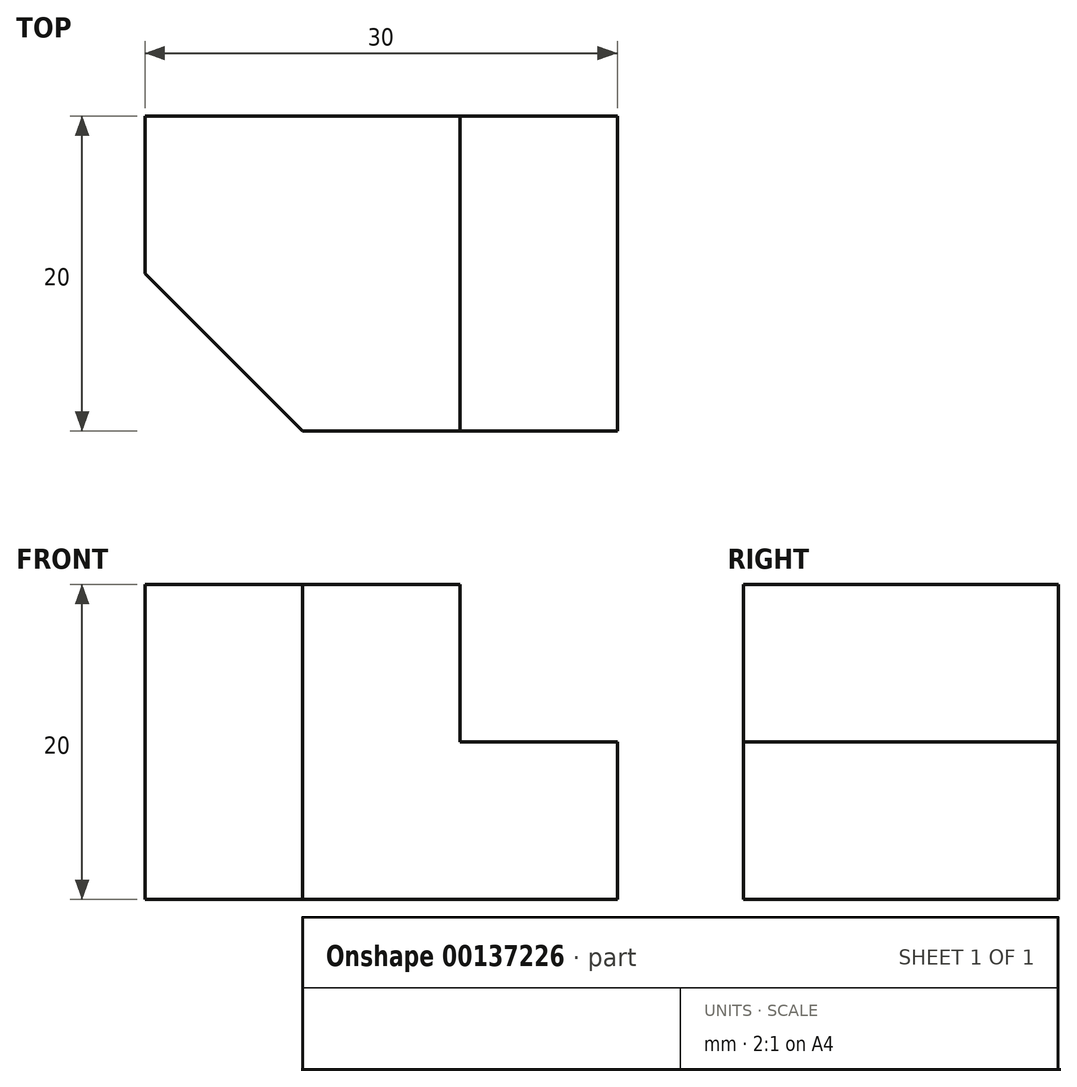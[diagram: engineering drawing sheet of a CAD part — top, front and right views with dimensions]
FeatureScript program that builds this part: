
annotation { "Feature Type Name" : "Feature", "Feature Type Description" : "" }
export const myFeature = defineFeature(function(context is Context, id is Id, definition is map)
    precondition{}
    {
        {
            var Q0;
            Q0=qCreatedBy(makeId("Front.planeOp"),FACE);
            var sketch = newSketch(context, id + "F0", { "sketchPlane" : qUnion([Q0])});
            skLineSegment(sketch, "E0", {"start": v(0, 0) * mm, "end": v(30, 0) * mm});
            skLineSegment(sketch, "E1", {"start": v(30, 0) * mm, "end": v(30, 10) * mm});
            skLineSegment(sketch, "E2", {"start": v(30, 10) * mm, "end": v(20, 10) * mm});
            skLineSegment(sketch, "E3", {"start": v(20, 10) * mm, "end": v(20, 20) * mm});
            skLineSegment(sketch, "E4", {"start": v(20, 20) * mm, "end": v(0, 20) * mm});
            skLineSegment(sketch, "E5", {"start": v(0, 20) * mm, "end": v(0, 0) * mm});
            skSolve(sketch);
        }
        {
            var Q0;
            Q0=makeQuery(id+"F0.imprint","IMPRINT",FACE,{"disambiguationData":[TD([[makeQuery(id+"F0.imprint","IMPRINT",EDGE,{"derivedFrom":sQuery(id+"F0.wireOp",EDGE,"E0")}),1.0]])]});
            extrude(context, id + "F1", {"entities" : qUnion([Q0]), "oppositeDirection" : true, "depth" : 20 * mm});
        }
        {
            var Q0;
            Q0=makeQuery(id+"F1.opExtrude","SWEPT_FACE",FACE,{"disambiguationData":[OSD([sQuery(id+"F0.wireOp",EDGE,"E4")])]});
            var sketch = newSketch(context, id + "F2", { "sketchPlane" : qUnion([Q0])});
            skLineSegment(sketch, "E6", {"start": v(10, 0) * mm, "end": v(0, 10) * mm});
            skSolve(sketch);
        }
        {
            var Q0;
            {var subQ0=sQuery(id+"F2.wireOp",EDGE,"E6");Q0=makeQuery(id+"F2.imprint","IMPRINT",FACE,{"disambiguationData":[TD([[makeQuery(id+"F2.imprint","IMPRINT",EDGE,{"derivedFrom":subQ0}),1.0]])]});}
            extrude(context, id + "F3", {"entities" : qUnion([Q0]), "operationType" : NewBodyOperationType.REMOVE, "oppositeDirection" : true, "depth" : 25 * mm});
        }
    });
